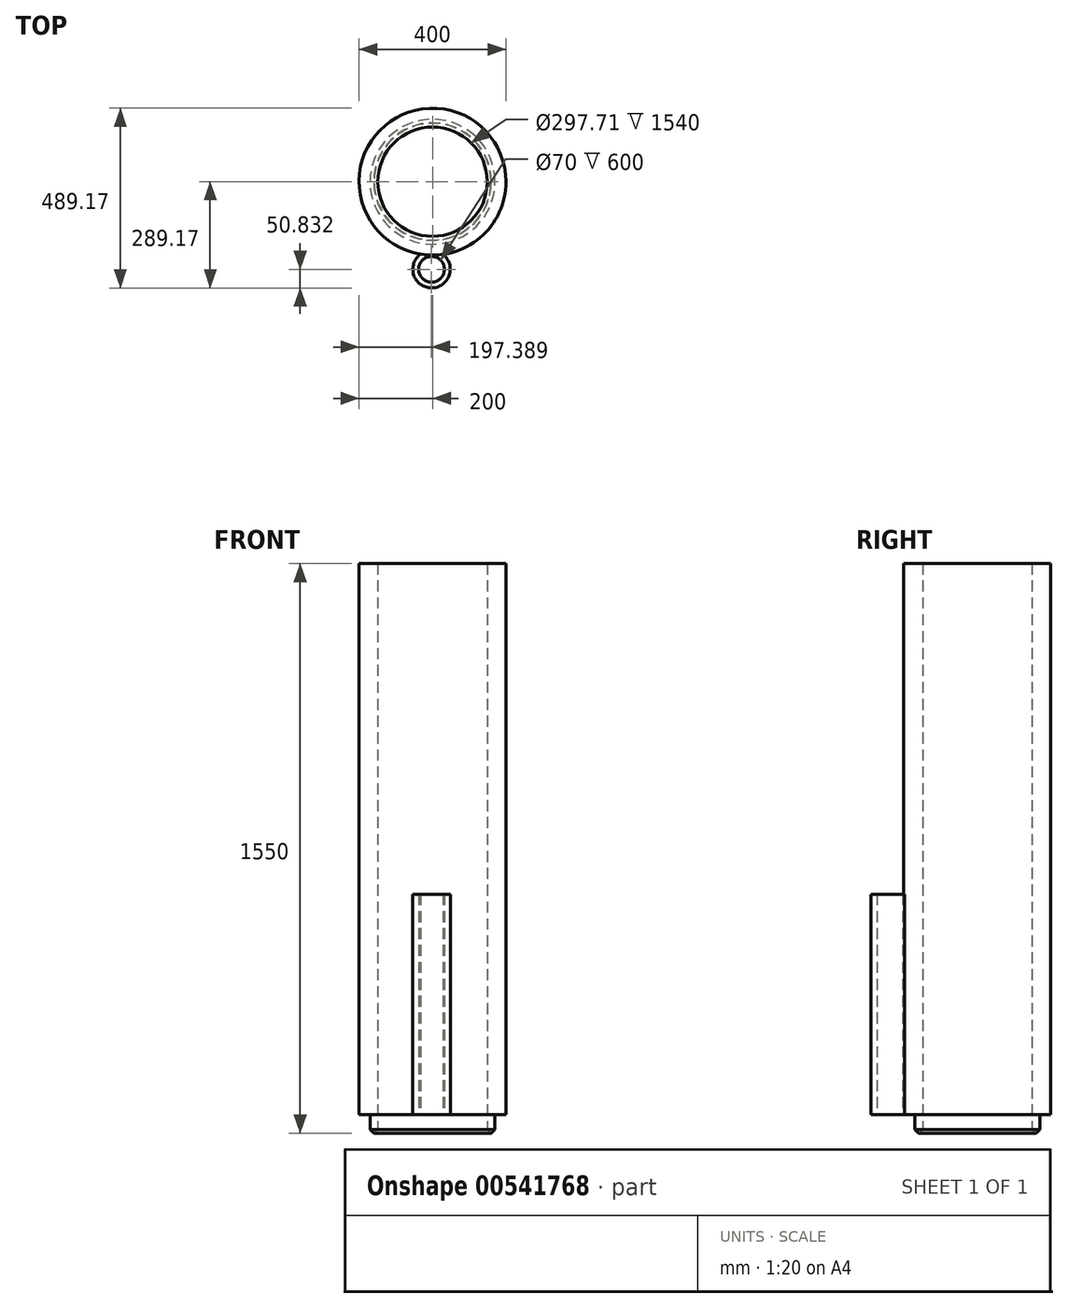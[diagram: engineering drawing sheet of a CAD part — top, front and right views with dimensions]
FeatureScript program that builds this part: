
annotation { "Feature Type Name" : "Feature", "Feature Type Description" : "" }
export const myFeature = defineFeature(function(context is Context, id is Id, definition is map)
    precondition{}
    {
        {
            var Q0;
            Q0=qCreatedBy(makeId("Top.planeOp"),FACE);
            var sketch = newSketch(context, id + "F0", { "sketchPlane" : qUnion([Q0])});
            skCircle(sketch, "E0", {"center": v(0, 0) * mm, "radius": 170 * mm});
            skCircle(sketch, "E1", {"center": v(0, 0) * mm, "radius": 148.86 * mm});
            skSolve(sketch);
        }
        {
            var Q0;
            Q0 = qSketchRegion(id + "F0", true);
            extrude(context, id + "F1", {"entities" : qUnion([Q0]), "depth" : 50 * mm, "offsetDistance" : 25 * mm});
        }
        {
            var Q0;
            Q0=makeQuery(id+"F1.opExtrude","CAP_FACE",FACE,{"disambiguationData":[OSD([sQuery(id+"F0.wireOp",EDGE,"E0"),sQuery(id+"F0.wireOp",EDGE,"E1")])],"isStart":false});
            var sketch = newSketch(context, id + "F2", { "sketchPlane" : qUnion([Q0])});
            skCircle(sketch, "E2", {"center": v(0, 0) * mm, "radius": 200 * mm});
            skCircle(sketch, "E3", {"center": v(0, 0) * mm, "radius": 170 * mm});
            skSolve(sketch);
        }
        {
            var Q0;
            Q0=makeQuery(id+"F1.opExtrude","CAP_FACE",FACE,{"disambiguationData":[OSD([sQuery(id+"F0.wireOp",EDGE,"E0"),sQuery(id+"F0.wireOp",EDGE,"E1")])],"isStart":false});
            var Q1;
            Q1 = qSketchRegion(id + "F2", true);
            extrude(context, id + "F3", {"entities" : qUnion([Q0, Q1]), "operationType" : NewBodyOperationType.ADD, "depth" : 1500 * mm, "offsetDistance" : 25 * mm});
        }
        {
            var Q0;
            Q0=makeQuery(id+"F1.opExtrude","CAP_FACE",FACE,{"disambiguationData":[OSD([sQuery(id+"F0.wireOp",EDGE,"E0"),sQuery(id+"F0.wireOp",EDGE,"E1")])],"isStart":true});
            chamfer(context, id + "F4", {"entities" : qUnion([Q0]), "width" : 10 * mm, "tangentPropagation" : true});
        }
        {
            var Q0;
            Q0=makeQuery(id+"F3.boolean.opBoolean","MERGE",FACE,{"derivedFrom":[makeQuery(id+"F3.opExtrude","CAP_FACE",FACE,{"disambiguationData":[OSD([sQuery(id+"F0.wireOp",EDGE,"E0"),sQuery(id+"F0.wireOp",EDGE,"E1")])],"isStart":true}),makeQuery(id+"F3.opExtrude","CAP_FACE",FACE,{"disambiguationData":[OSD([sQuery(id+"F2.wireOp",EDGE,"E2"),sQuery(id+"F2.wireOp",EDGE,"E3")])],"isStart":true})]});
            var sketch = newSketch(context, id + "F5", { "sketchPlane" : qUnion([Q0])});
            skArc(sketch, "E4", {"start": v(28.3, 197.99) * mm, "mid": v(-3.17, 289.16) * mm, "end": v(-32.63, 197.32) * mm});
            skSolve(sketch);
        }
        {
            var Q0;
            Q0 = qSketchRegion(id + "F5", true);
            var Q1;
            {var subQ0=sQuery(id+"F5.wireOp",EDGE,"E4");Q1=makeQuery(id+"F5.imprint","IMPRINT",FACE,{"disambiguationData":[TD([[makeQuery(id+"F5.imprint","IMPRINT",EDGE,{"derivedFrom":subQ0}),1.0]])]});}
            extrude(context, id + "F6", {"entities" : qUnion([Q0, Q1]), "operationType" : NewBodyOperationType.ADD, "oppositeDirection" : true, "depth" : 600 * mm, "offsetDistance" : 25 * mm});
        }
        {
            var Q0;
            {var subQ0=sQuery(id+"F2.wireOp",EDGE,"E2");Q0=makeQuery(id+"F6.boolean.opBoolean","MERGE",FACE,{"derivedFrom":[makeQuery(id+"F3.boolean.opBoolean","MERGE",FACE,{"derivedFrom":[makeQuery(id+"F3.opExtrude","CAP_FACE",FACE,{"disambiguationData":[OSD([sQuery(id+"F0.wireOp",EDGE,"E0"),sQuery(id+"F0.wireOp",EDGE,"E1")])],"isStart":true}),makeQuery(id+"F3.opExtrude","CAP_FACE",FACE,{"disambiguationData":[OSD([subQ0,sQuery(id+"F2.wireOp",EDGE,"E3")])],"isStart":true})]}),makeQuery(id+"F6.opExtrude","CAP_FACE",FACE,{"disambiguationData":[OSD([subQ0,sQuery(id+"F5.wireOp",EDGE,"E4")])],"isStart":true})]});}
            var sketch = newSketch(context, id + "F7", { "sketchPlane" : qUnion([Q0])});
            skCircle(sketch, "E5", {"center": v(-2.61, 238.34) * mm, "radius": 35 * mm});
            skSolve(sketch);
        }
        {
            var Q0;
            Q0=makeQuery(id+"F7.imprint","IMPRINT",FACE,{"disambiguationData":[TD([[makeQuery(id+"F7.imprint","IMPRINT",EDGE,{"derivedFrom":sQuery(id+"F7.wireOp",EDGE,"E5")}),1.0]])]});
            extrude(context, id + "F8", {"entities" : qUnion([Q0]), "operationType" : NewBodyOperationType.REMOVE, "oppositeDirection" : true, "depth" : 600 * mm, "offsetDistance" : 25 * mm});
        }
    });
